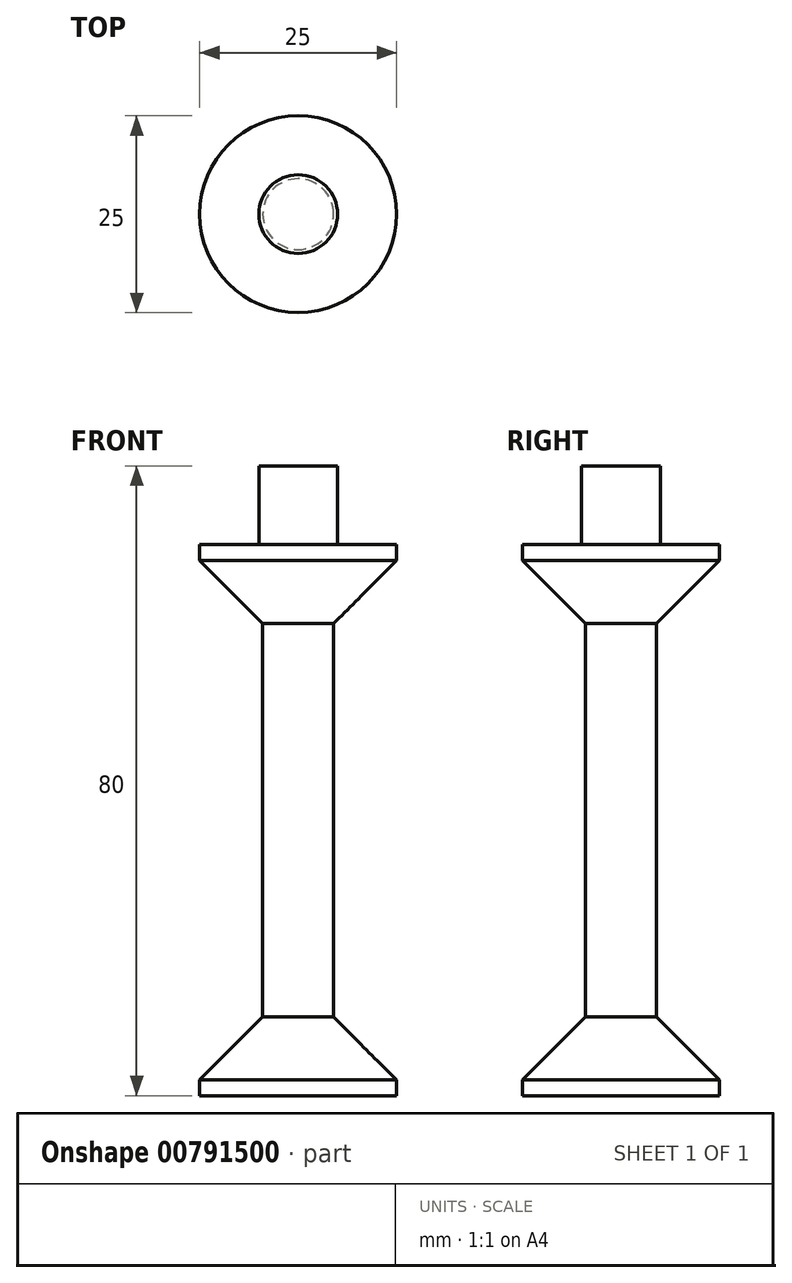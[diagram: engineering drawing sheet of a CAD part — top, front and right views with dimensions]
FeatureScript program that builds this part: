
annotation { "Feature Type Name" : "Feature", "Feature Type Description" : "" }
export const myFeature = defineFeature(function(context is Context, id is Id, definition is map)
    precondition{}
    {
        {
            var Q0;
            Q0=qCreatedBy(makeId("Top.planeOp"),FACE);
            var sketch = newSketch(context, id + "F0", { "sketchPlane" : qUnion([Q0])});
            skCircle(sketch, "E0", {"center": v(0, 0) * mm, "radius": 12.5 * mm});
            skSolve(sketch);
        }
        {
            var Q0;
            Q0 = qSketchRegion(id + "F0", true);
            var Q1;
            Q1=makeQuery(id+"F0.imprint","IMPRINT",FACE,{"disambiguationData":[TD([[makeQuery(id+"F0.imprint","IMPRINT",EDGE,{"derivedFrom":sQuery(id+"F0.wireOp",EDGE,"E0")}),1.0]])]});
            extrude(context, id + "F1", {"entities" : qUnion([Q0, Q1]), "depth" : 2 * mm, "offsetDistance" : 25 * mm});
        }
        {
            var Q0;
            Q0=makeQuery(id+"F1.opExtrude","CAP_FACE",FACE,{"disambiguationData":[OSD([sQuery(id+"F0.wireOp",EDGE,"E0")])],"isStart":false});
            extrude(context, id + "F2", {"entities" : qUnion([Q0]), "operationType" : NewBodyOperationType.ADD, "depth" : 8 * mm, "offsetDistance" : 25 * mm, "hasDraft" : true, "draftAngle" : 45 * degree, "draftPullDirection" : true});
        }
        {
            var Q0;
            Q0=makeQuery(id+"F2.opExtrude","CAP_FACE",FACE,{"disambiguationData":[OSD([sQuery(id+"F0.wireOp",EDGE,"E0")])],"isStart":false});
            extrude(context, id + "F3", {"entities" : qUnion([Q0]), "operationType" : NewBodyOperationType.ADD, "depth" : 25 * mm, "offsetDistance" : 25 * mm});
        }
        {
            var Q0;
            Q0=makeQuery(id+"F1.opExtrude","SWEPT_BODY",BODY,{"disambiguationData":[OSD([sQuery(id+"F0.wireOp",EDGE,"E0")])]});
            var Q1;
            Q1=makeQuery(id+"F3.opExtrude","CAP_FACE",FACE,{"disambiguationData":[OSD([sQuery(id+"F0.wireOp",EDGE,"E0")])],"isStart":false});
            mirror(context, id + "F4", {"operationType" : NewBodyOperationType.ADD, "entities" : qUnion([Q0]), "mirrorPlane" : qUnion([Q1])});
        }
        {
            var Q0;
            Q0=makeQuery(id+"F4.opPattern","COPY",FACE,{"derivedFrom":makeQuery(id+"F1.opExtrude","CAP_FACE",FACE,{"disambiguationData":[OSD([sQuery(id+"F0.wireOp",EDGE,"E0")])],"isStart":true}),"instanceName":"1"});
            var sketch = newSketch(context, id + "F5", { "sketchPlane" : qUnion([Q0])});
            skCircle(sketch, "E1", {"center": v(0, 0) * mm, "radius": 5 * mm});
            skSolve(sketch);
        }
        {
            var Q0;
            Q0 = qSketchRegion(id + "F5", true);
            var Q1;
            Q1=makeQuery(id+"F5.imprint","IMPRINT",FACE,{"disambiguationData":[TD([[makeQuery(id+"F5.imprint","IMPRINT",EDGE,{"derivedFrom":sQuery(id+"F5.wireOp",EDGE,"E1")}),1.0]])]});
            extrude(context, id + "F6", {"entities" : qUnion([Q0, Q1]), "operationType" : NewBodyOperationType.ADD, "depth" : 10 * mm, "offsetDistance" : 25 * mm});
        }
    });
